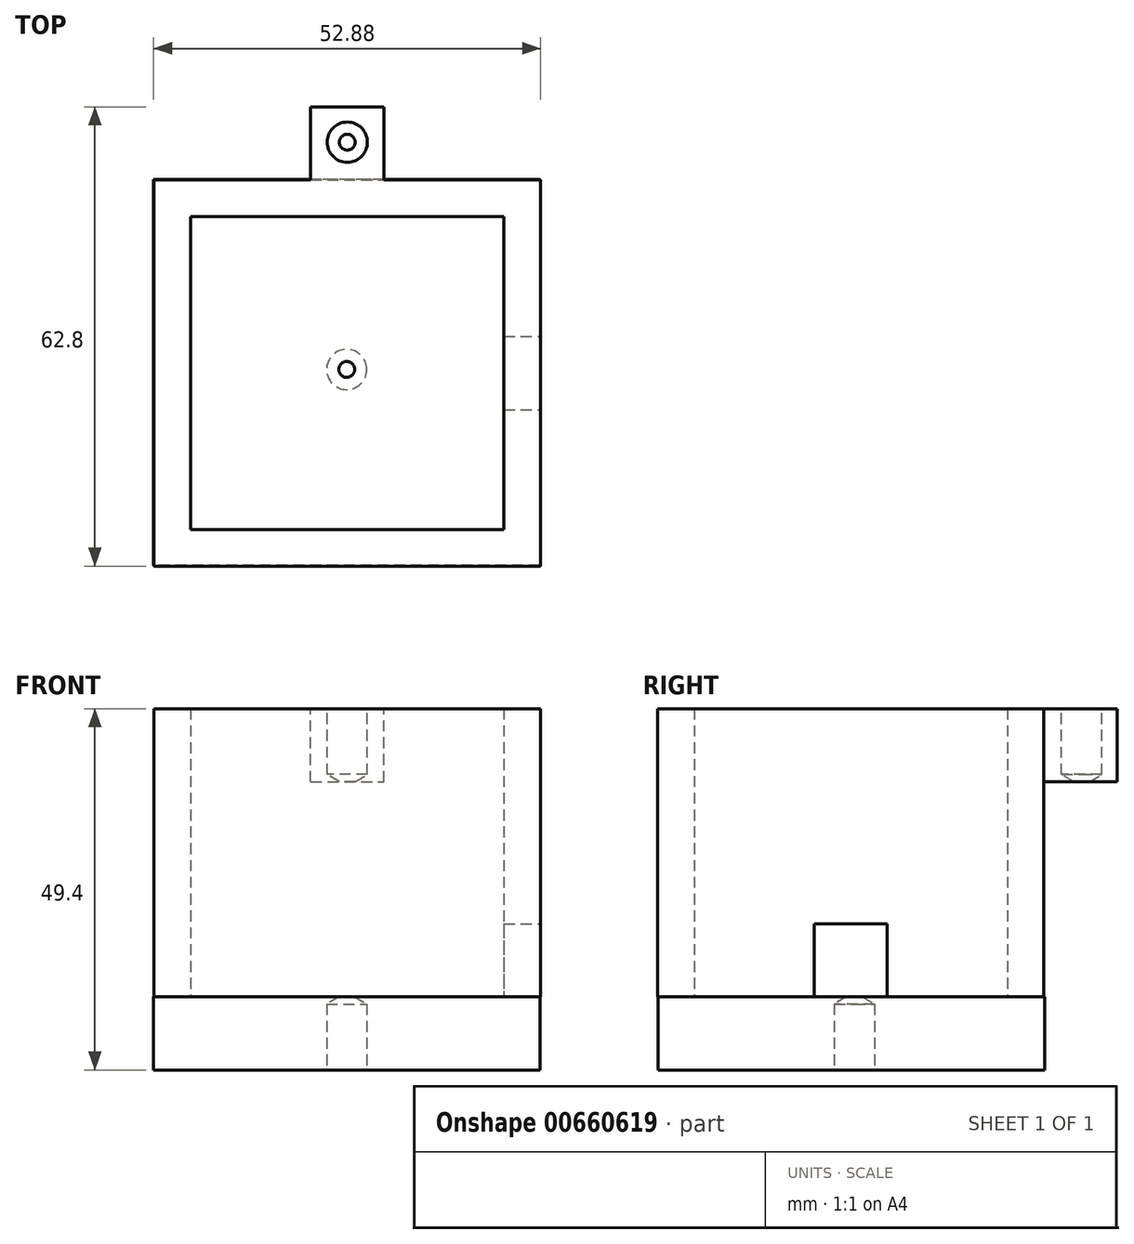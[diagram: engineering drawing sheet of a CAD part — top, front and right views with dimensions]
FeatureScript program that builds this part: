
annotation { "Feature Type Name" : "Feature", "Feature Type Description" : "" }
export const myFeature = defineFeature(function(context is Context, id is Id, definition is map)
    precondition{}
    {
        {
            var Q0;
            Q0=qCreatedBy(makeId("Top.planeOp"),FACE);
            var sketch = newSketch(context, id + "F0", { "sketchPlane" : qUnion([Q0])});
            skLineSegment(sketch, "E0.bottom", {"start": v(9, -2.88) * mm, "end": v(51.8, -2.88) * mm});
            skLineSegment(sketch, "E0.top", {"start": v(9, 39.92) * mm, "end": v(51.8, 39.92) * mm});
            skLineSegment(sketch, "E0.left", {"start": v(9, -2.88) * mm, "end": v(9, 39.92) * mm});
            skLineSegment(sketch, "E0.right", {"start": v(51.8, -2.88) * mm, "end": v(51.8, 39.92) * mm});
            skLineSegment(sketch, "E1.bottom", {"start": v(4, -7.88) * mm, "end": v(56.8, -7.88) * mm});
            skLineSegment(sketch, "E1.top", {"start": v(4, 44.92) * mm, "end": v(56.8, 44.92) * mm});
            skLineSegment(sketch, "E1.left", {"start": v(4, -7.88) * mm, "end": v(4, 44.92) * mm});
            skLineSegment(sketch, "E1.right", {"start": v(56.8, -7.88) * mm, "end": v(56.8, 44.92) * mm});
            skSolve(sketch);
        }
        {
            var Q0;
            Q0 = qSketchRegion(id + "F0", true);
            extrude(context, id + "F1", {"entities" : qUnion([Q0]), "depth" : 39.4 * mm, "offsetDistance" : 25 * mm});
        }
        {
            var Q0;
            Q0=qCreatedBy(makeId("Top.planeOp"),FACE);
            var sketch = newSketch(context, id + "F2", { "sketchPlane" : qUnion([Q0])});
            skLineSegment(sketch, "E2.bottom", {"start": v(56.73, 45) * mm, "end": v(3.93, 45) * mm});
            skLineSegment(sketch, "E2.top", {"start": v(56.73, -7.8) * mm, "end": v(3.93, -7.8) * mm});
            skLineSegment(sketch, "E2.left", {"start": v(56.73, 45) * mm, "end": v(56.73, -7.8) * mm});
            skLineSegment(sketch, "E2.right", {"start": v(3.93, 45) * mm, "end": v(3.93, -7.8) * mm});
            skSolve(sketch);
        }
        {
            var Q0;
            Q0 = qSketchRegion(id + "F2", true);
            extrude(context, id + "F3", {"entities" : qUnion([Q0]), "operationType" : NewBodyOperationType.ADD, "depth" : -10 * mm, "offsetDistance" : 25 * mm});
        }
        {
            var Q0;
            Q0=makeQuery(id+"F1.opExtrude","SWEPT_FACE",FACE,{"disambiguationData":[OSD([sQuery(id+"F0.wireOp",EDGE,"E1.right")])]});
            var sketch = newSketch(context, id + "F4", { "sketchPlane" : qUnion([Q0])});
            skLineSegment(sketch, "E3.bottom", {"start": v(13.52, 0) * mm, "end": v(23.52, 0) * mm});
            skLineSegment(sketch, "E3.top", {"start": v(13.52, 10) * mm, "end": v(23.52, 10) * mm});
            skLineSegment(sketch, "E3.left", {"start": v(13.52, 0) * mm, "end": v(13.52, 10) * mm});
            skLineSegment(sketch, "E3.right", {"start": v(23.52, 0) * mm, "end": v(23.52, 10) * mm});
            skSolve(sketch);
        }
        {
            var Q0;
            Q0=makeQuery(id+"F4.imprint","IMPRINT",FACE,{"disambiguationData":[TD([[makeQuery(id+"F4.imprint","IMPRINT",EDGE,{"derivedFrom":sQuery(id+"F4.wireOp",EDGE,"E3.bottom")}),1.0]])]});
            extrude(context, id + "F5", {"entities" : qUnion([Q0]), "operationType" : NewBodyOperationType.REMOVE, "oppositeDirection" : true, "depth" : 25 * mm, "offsetDistance" : 25 * mm});
        }
        {
            var Q0;
            Q0=makeQuery(id+"F1.opExtrude","CAP_FACE",FACE,{"disambiguationData":[OSD([sQuery(id+"F0.wireOp",EDGE,"E0.bottom"),sQuery(id+"F0.wireOp",EDGE,"E0.top"),sQuery(id+"F0.wireOp",EDGE,"E0.left"),sQuery(id+"F0.wireOp",EDGE,"E0.right"),sQuery(id+"F0.wireOp",EDGE,"E1.bottom"),sQuery(id+"F0.wireOp",EDGE,"E1.top"),sQuery(id+"F0.wireOp",EDGE,"E1.left"),sQuery(id+"F0.wireOp",EDGE,"E1.right")])],"isStart":false});
            var sketch = newSketch(context, id + "F6", { "sketchPlane" : qUnion([Q0])});
            skLineSegment(sketch, "E4.bottom", {"start": v(25.4, 44.92) * mm, "end": v(35.4, 44.92) * mm});
            skLineSegment(sketch, "E4.top", {"start": v(25.4, 54.92) * mm, "end": v(35.4, 54.92) * mm});
            skLineSegment(sketch, "E4.left", {"start": v(25.4, 44.92) * mm, "end": v(25.4, 54.92) * mm});
            skLineSegment(sketch, "E4.right", {"start": v(35.4, 44.92) * mm, "end": v(35.4, 54.92) * mm});
            skSolve(sketch);
        }
        {
            var Q0;
            Q0 = qSketchRegion(id + "F6", true);
            extrude(context, id + "F7", {"entities" : qUnion([Q0]), "operationType" : NewBodyOperationType.ADD, "depth" : -10 * mm, "offsetDistance" : 25 * mm});
        }
        {
            var Q0;
            Q0=makeQuery(id+"F7.boolean.opBoolean","MERGE",FACE,{"derivedFrom":[makeQuery(id+"F1.opExtrude","CAP_FACE",FACE,{"disambiguationData":[OSD([sQuery(id+"F0.wireOp",EDGE,"E0.bottom"),sQuery(id+"F0.wireOp",EDGE,"E0.top"),sQuery(id+"F0.wireOp",EDGE,"E0.left"),sQuery(id+"F0.wireOp",EDGE,"E0.right"),sQuery(id+"F0.wireOp",EDGE,"E1.bottom"),sQuery(id+"F0.wireOp",EDGE,"E1.top"),sQuery(id+"F0.wireOp",EDGE,"E1.left"),sQuery(id+"F0.wireOp",EDGE,"E1.right")])],"isStart":false}),makeQuery(id+"F7.opExtrude","CAP_FACE",FACE,{"disambiguationData":[OSD([sQuery(id+"F6.wireOp",EDGE,"E4.bottom"),sQuery(id+"F6.wireOp",EDGE,"E4.top"),sQuery(id+"F6.wireOp",EDGE,"E4.left"),sQuery(id+"F6.wireOp",EDGE,"E4.right")])],"isStart":true})]});
            var sketch = newSketch(context, id + "F8", { "sketchPlane" : qUnion([Q0])});
            skCircle(sketch, "E5", {"center": v(30.4, 50.08) * mm, "radius": 3 * mm});
            skSolve(sketch);
        }
        {
            var Q0;
            Q0=sQuery(id+"F8.wireOp",VERTEX,"E5.center");
            var Q1;
            Q1=makeQuery(id+"F1.opExtrude","SWEPT_BODY",BODY,{"disambiguationData":[OSD([sQuery(id+"F0.wireOp",EDGE,"E0.bottom"),sQuery(id+"F0.wireOp",EDGE,"E0.top"),sQuery(id+"F0.wireOp",EDGE,"E0.left"),sQuery(id+"F0.wireOp",EDGE,"E0.right"),sQuery(id+"F0.wireOp",EDGE,"E1.bottom"),sQuery(id+"F0.wireOp",EDGE,"E1.top"),sQuery(id+"F0.wireOp",EDGE,"E1.left"),sQuery(id+"F0.wireOp",EDGE,"E1.right")])]});
            hole(context, id + "F9", {"style" : HoleStyle.SIMPLE, "endStyle" : HoleEndStyle.BLIND, "holeDiameter" : 5.5 * mm, "majorDiameter" : 5 * mm, "holeDepth" : 9 * mm, "isTappedThrough" : true, "tappedDepth" : 12 * mm, "tapClearance" : 3, "locations" : qUnion([Q0]), "scope" : qUnion([Q1])});
        }
        {
            var Q0;
            Q0=makeQuery(id+"F3.opExtrude","CAP_FACE",FACE,{"disambiguationData":[OSD([sQuery(id+"F2.wireOp",EDGE,"E2.bottom"),sQuery(id+"F2.wireOp",EDGE,"E2.top"),sQuery(id+"F2.wireOp",EDGE,"E2.left"),sQuery(id+"F2.wireOp",EDGE,"E2.right")])],"isStart":false});
            var sketch = newSketch(context, id + "F10", { "sketchPlane" : qUnion([Q0])});
            skCircle(sketch, "E6", {"center": v(30.33, -19) * mm, "radius": 3 * mm});
            skSolve(sketch);
        }
        {
            var Q0;
            Q0=sQuery(id+"F10.wireOp",VERTEX,"E6.center");
            var Q1;
            Q1=makeQuery(id+"F1.opExtrude","SWEPT_BODY",BODY,{"disambiguationData":[OSD([sQuery(id+"F0.wireOp",EDGE,"E0.bottom"),sQuery(id+"F0.wireOp",EDGE,"E0.top"),sQuery(id+"F0.wireOp",EDGE,"E0.left"),sQuery(id+"F0.wireOp",EDGE,"E0.right"),sQuery(id+"F0.wireOp",EDGE,"E1.bottom"),sQuery(id+"F0.wireOp",EDGE,"E1.top"),sQuery(id+"F0.wireOp",EDGE,"E1.left"),sQuery(id+"F0.wireOp",EDGE,"E1.right")])]});
            hole(context, id + "F11", {"style" : HoleStyle.SIMPLE, "endStyle" : HoleEndStyle.BLIND, "holeDiameter" : 5.5 * mm, "majorDiameter" : 5 * mm, "holeDepth" : 9 * mm, "isTappedThrough" : true, "tappedDepth" : 12 * mm, "tapClearance" : 3, "locations" : qUnion([Q0]), "scope" : qUnion([Q1])});
        }
    });
